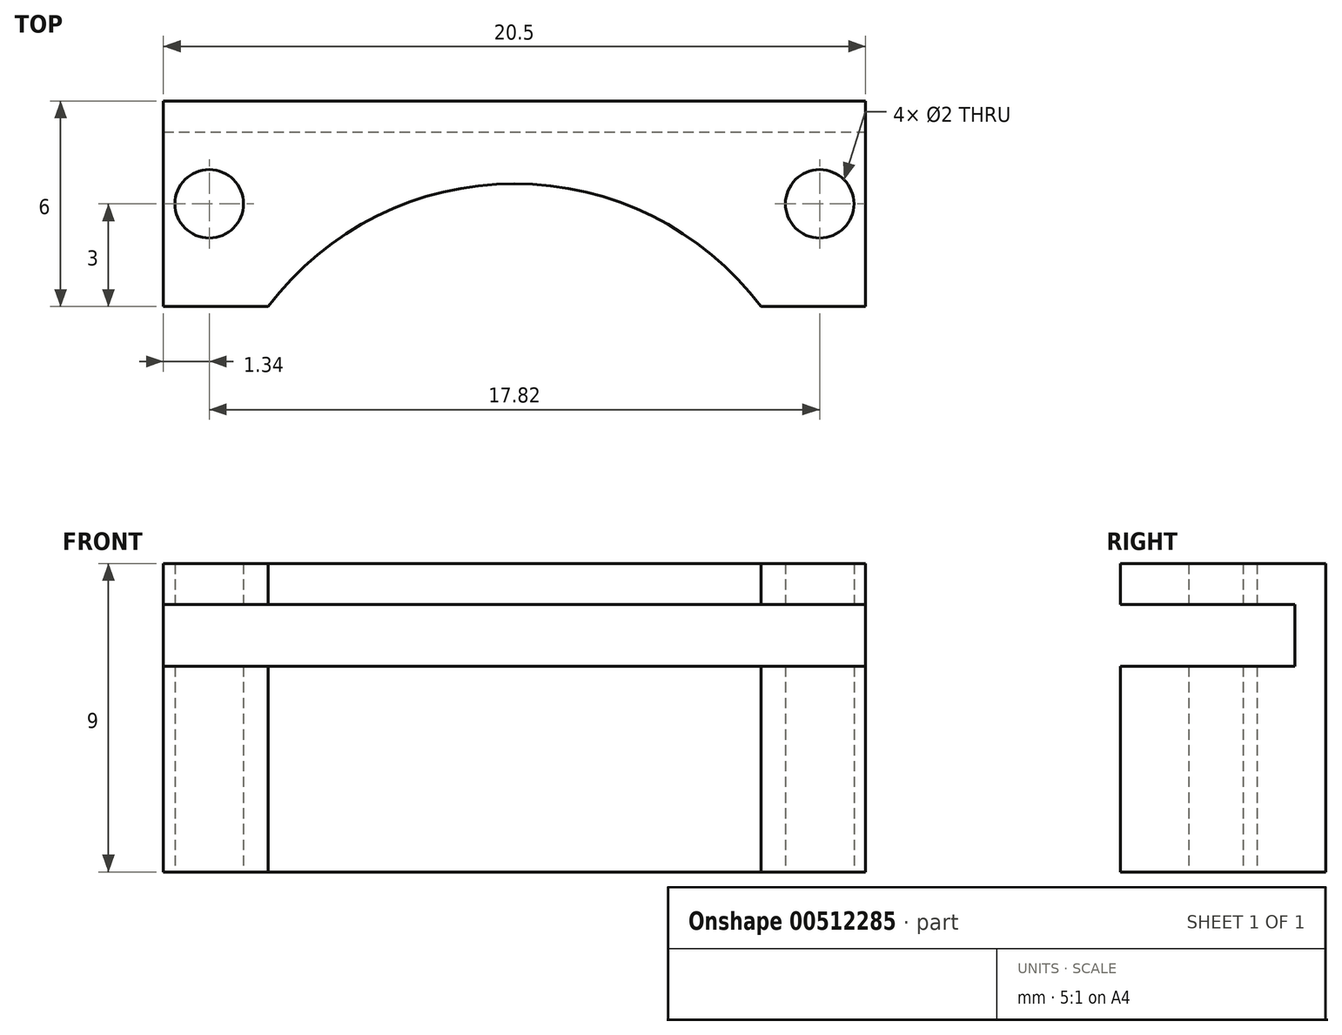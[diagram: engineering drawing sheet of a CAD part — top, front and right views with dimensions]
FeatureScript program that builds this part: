
annotation { "Feature Type Name" : "Feature", "Feature Type Description" : "" }
export const myFeature = defineFeature(function(context is Context, id is Id, definition is map)
    precondition{}
    {
        {
            var Q0;
            Q0=qCreatedBy(makeId("Top.planeOp"),FACE);
            var sketch = newSketch(context, id + "F0", { "sketchPlane" : qUnion([Q0])});
            skCircle(sketch, "E0", {"center": v(8.91, 0) * mm, "radius": 1 * mm});
            skLineSegment(sketch, "E1", {"start": v(0, 7.92) * mm, "end": v(0, -11.2) * mm, "construction": true});
            skLineSegment(sketch, "E2", {"start": v(-8.91, 0) * mm, "end": v(8.91, 0) * mm, "construction": true});
            skCircle(sketch, "E3", {"center": v(-8.91, 0) * mm, "radius": 1 * mm});
            skLineSegment(sketch, "E4.bottom", {"start": v(-10.25, 3) * mm, "end": v(10.25, 3) * mm});
            skLineSegment(sketch, "E4.top", {"start": v(-10.25, -3) * mm, "end": v(10.25, -3) * mm});
            skLineSegment(sketch, "E4.left", {"start": v(-10.25, 3) * mm, "end": v(-10.25, -3) * mm});
            skLineSegment(sketch, "E4.right", {"start": v(10.25, 3) * mm, "end": v(10.25, -3) * mm});
            skSolve(sketch);
        }
        {
            var Q0;
            Q0 = qSketchRegion(id + "F0", true);
            extrude(context, id + "F1", {"entities" : qUnion([Q0]), "depth" : 9 * mm, "offsetDistance" : 25 * mm});
        }
        {
            var Q0;
            Q0=makeQuery(id+"F1.opExtrude","SWEPT_FACE",FACE,{"disambiguationData":[OSD([sQuery(id+"F0.wireOp",EDGE,"E4.right")])]});
            var sketch = newSketch(context, id + "F2", { "sketchPlane" : qUnion([Q0])});
            skLineSegment(sketch, "E5.0", {"start": v(-3, 7.8) * mm, "end": v(-3, 6) * mm});
            skLineSegment(sketch, "E6", {"start": v(-3, 7.8) * mm, "end": v(2.1, 7.8) * mm});
            skLineSegment(sketch, "E7", {"start": v(2.1, 7.8) * mm, "end": v(2.1, 6) * mm});
            skLineSegment(sketch, "E8", {"start": v(2.1, 6) * mm, "end": v(-3, 6) * mm});
            skPoint(sketch, "E9.orphan", {"position": v(-3, 0) * mm});
            skPoint(sketch, "E10.orphan", {"position": v(-3, 9) * mm});
            skLineSegment(sketch, "E11", {"start": v(0, 9) * mm, "end": v(0, 0) * mm, "construction": true});
            skSolve(sketch);
        }
        {
            var Q0;
            Q0 = qSketchRegion(id + "F2", true);
            extrude(context, id + "F3", {"entities" : qUnion([Q0]), "operationType" : NewBodyOperationType.REMOVE, "endBound" : BoundingType.THROUGH_ALL, "oppositeDirection" : true, "depth" : 25 * mm, "offsetDistance" : 25 * mm});
        }
        {
            var Q0;
            Q0=makeQuery(id+"F1.opExtrude","CAP_FACE",FACE,{"disambiguationData":[OSD([sQuery(id+"F0.wireOp",EDGE,"E0"),sQuery(id+"F0.wireOp",EDGE,"E3"),sQuery(id+"F0.wireOp",EDGE,"E4.bottom"),sQuery(id+"F0.wireOp",EDGE,"E4.top"),sQuery(id+"F0.wireOp",EDGE,"E4.left"),sQuery(id+"F0.wireOp",EDGE,"E4.right")])],"isStart":true});
            var sketch = newSketch(context, id + "F4", { "sketchPlane" : qUnion([Q0])});
            skLineSegment(sketch, "E12", {"start": v(0, -3) * mm, "end": v(0, 8.4) * mm, "construction": true});
            skPoint(sketch, "E12.endSnap0", {"position": v(0, -3) * mm});
            skCircle(sketch, "E13", {"center": v(0, 8.4) * mm, "radius": 9 * mm});
            skSolve(sketch);
        }
        {
            var Q0;
            Q0 = qSketchRegion(id + "F4", true);
            extrude(context, id + "F5", {"entities" : qUnion([Q0]), "operationType" : NewBodyOperationType.REMOVE, "oppositeDirection" : true, "depth" : 25 * mm, "offsetDistance" : 25 * mm});
        }
    });
